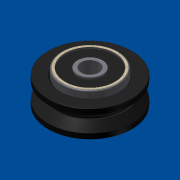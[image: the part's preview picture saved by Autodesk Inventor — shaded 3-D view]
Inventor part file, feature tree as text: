
AUTODESK INVENTOR PART (.ipt)
format: ipt  version: 2013 (Build 170138000, 138)  size: 254,976 bytes
history: native  units: in
note: dims shown in document units (in); Inventor stores cm internally (conversion verified against a paired STEP export)
features: other x6, extrude x2, sketch x2
ambient origin geometry x8: Origin, YZ Plane, XZ Plane, XY Plane, X Axis, Y Axis, Z Axis, Center Point
bodies: Solid1 (feature_tree)
feature tree (10):
  other  "MSK01-05A"
  other  "B17021.ipt:1"
  other  "BEARING_5_16_5.ipt:1"
  other  "BEARING_5_16_5.ipt:2"
  other  "MSK01-05A_Bodies"
  extrude  "Extrusion1"  Depth=0.0001in TaperAngle=0.0deg
  extrude  "Extrusion2"  [1 undecoded]
  other  "Srf1"
  sketch  "Sketch1"  dims[d0=0.3937in d1=0.0001in d2=0.0in]
  sketch  "Sketch2"  dims[d3=0.0001in d4=0.0in]
note: 1 required parameter value undecoded (feature->parameter linkage not recoverable at this tier; creation-order binding heuristic only, values carry confidence <= 0.55)
